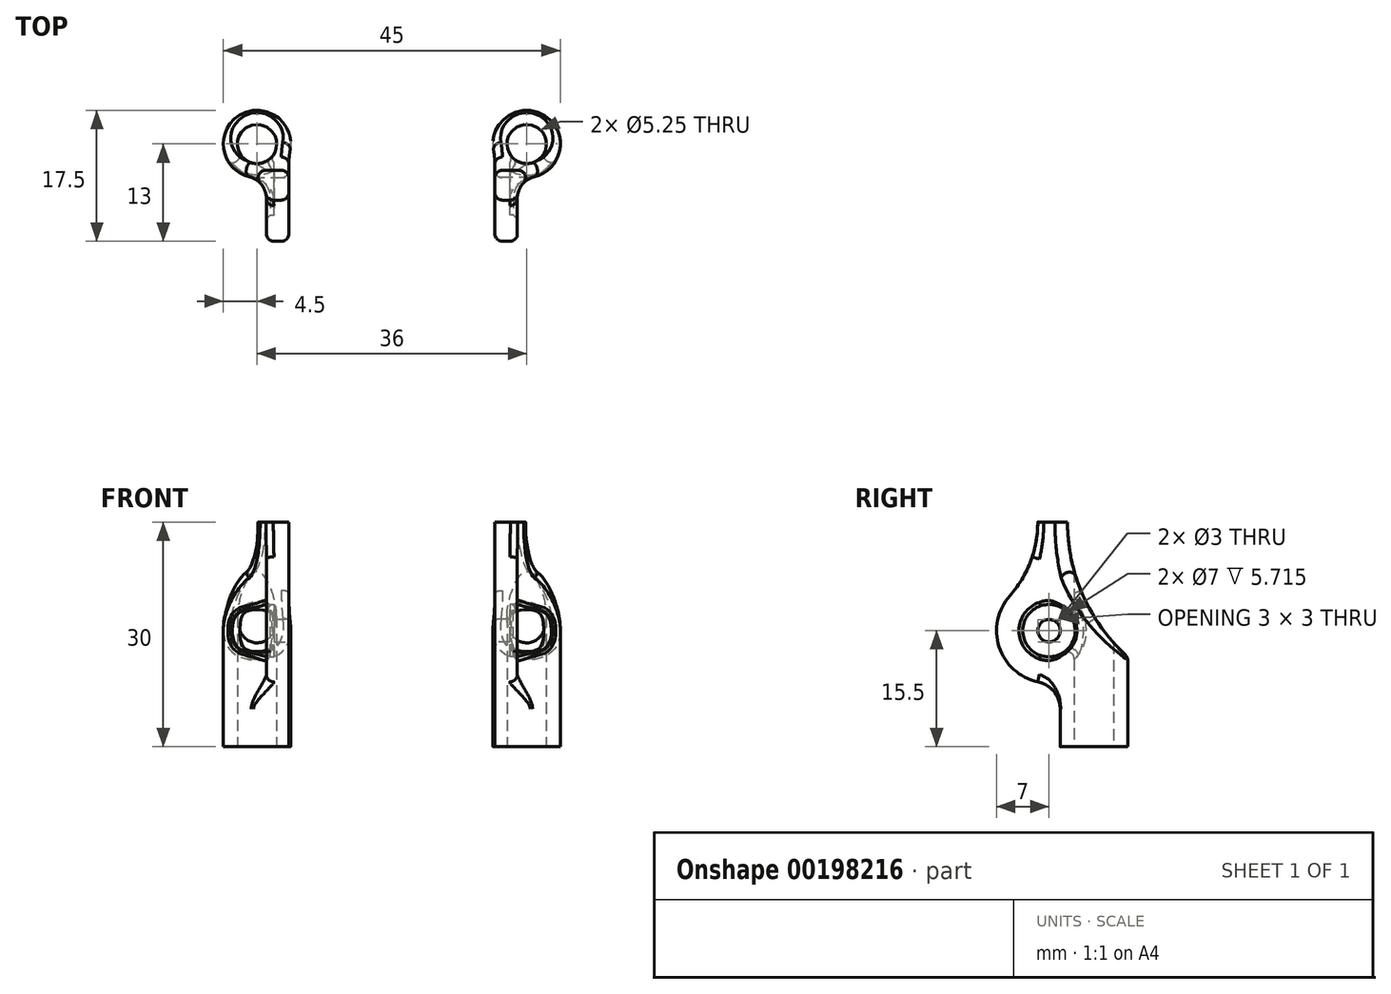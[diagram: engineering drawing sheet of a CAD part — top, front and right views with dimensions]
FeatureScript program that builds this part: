
annotation { "Feature Type Name" : "Feature", "Feature Type Description" : "" }
export const myFeature = defineFeature(function(context is Context, id is Id, definition is map)
    precondition{}
    {
        {
            var Q0;
            Q0=qCreatedBy(makeId("Top.planeOp"),FACE);
            var sketch = newSketch(context, id + "F0", { "sketchPlane" : qUnion([Q0])});
            skLineSegment(sketch, "E0", {"start": v(-13.75, 33.32) * mm, "end": v(-13.75, 22.5) * mm});
            skLineSegment(sketch, "E1", {"start": v(-13.75, 22.5) * mm, "end": v(-16.75, 22.5) * mm});
            skLineSegment(sketch, "E2", {"start": v(-16.75, 22.5) * mm, "end": v(-16.75, 28.7) * mm});
            skCircle(sketch, "E3", {"center": v(-18, 36) * mm, "radius": 2.62 * mm});
            skArc(sketch, "E4", {"start": v(-13.58, 35.17) * mm, "mid": v(-20.45, 39.78) * mm, "end": v(-19.05, 31.62) * mm});
            skPoint(sketch, "E5.visualSharp", {"position": v(-13.75, 34.52) * mm});
            skArc(sketch, "E5.filletArc", {"start": v(-13.58, 35.17) * mm, "mid": v(-13.7, 34.25) * mm, "end": v(-13.75, 33.32) * mm});
            skPoint(sketch, "E6.visualSharp", {"position": v(-16.75, 31.68) * mm});
            skArc(sketch, "E6.filletArc", {"start": v(-16.75, 28.7) * mm, "mid": v(-17.4, 30.56) * mm, "end": v(-19.05, 31.62) * mm});
            skSolve(sketch);
        }
        {
            var Q0;
            Q0=qSketchRegion(id+"F0",true);
            extrude(context, id + "F1", {"entities" : qUnion([Q0]), "depth" : 25 * mm});
        }
        {
            var Q0;
            Q0=makeQuery(id+"F1.opExtrude","SWEPT_FACE",FACE,{"disambiguationData":[OSD([sQuery(id+"F0.wireOp",EDGE,"E0")])]});
            var sketch = newSketch(context, id + "F2", { "sketchPlane" : qUnion([Q0])});
            skCircle(sketch, "E7", {"center": v(30, 10.5) * mm, "radius": 1.5 * mm});
            skArc(sketch, "E8", {"start": v(32.5, 26) * mm, "mid": v(34.36, 15.6) * mm, "end": v(40.5, 7) * mm});
            skLineSegment(sketch, "E9", {"start": v(32.5, 26) * mm, "end": v(40.5, 26) * mm});
            skLineSegment(sketch, "E10", {"start": v(40.5, 26) * mm, "end": v(40.5, 7) * mm});
            skLineSegment(sketch, "E11", {"start": v(28.5, 30) * mm, "end": v(28.5, 25) * mm});
            skArc(sketch, "E12", {"start": v(24.76, 15.14) * mm, "mid": v(27.53, 19.73) * mm, "end": v(28.5, 25) * mm});
            skArc(sketch, "E13", {"start": v(24.76, 15.14) * mm, "mid": v(23.35, 8.31) * mm, "end": v(28.54, 3.65) * mm});
            skLineSegment(sketch, "E14", {"start": v(28.5, 30) * mm, "end": v(18.5, 30) * mm});
            skLineSegment(sketch, "E15", {"start": v(18.5, 30) * mm, "end": v(18.5, -2) * mm});
            skArc(sketch, "E16", {"start": v(31.5, 0) * mm, "mid": v(30.67, 2.35) * mm, "end": v(28.54, 3.65) * mm});
            skLineSegment(sketch, "E17", {"start": v(31.5, 0) * mm, "end": v(31.5, -2) * mm});
            skLineSegment(sketch, "E18", {"start": v(31.5, -2) * mm, "end": v(18.5, -2) * mm});
            skSolve(sketch);
        }
        {
            var Q0;
            Q0=qSketchRegion(id+"F2",true);
            extrude(context, id + "F3", {"entities" : qUnion([Q0]), "operationType" : NewBodyOperationType.REMOVE, "oppositeDirection" : true, "depth" : 25 * mm, "hasSecondDirection" : true, "secondDirectionOppositeDirection" : false, "secondDirectionDepth" : 25 * mm});
        }
        {
            var Q0;
            Q0=makeQuery(id+"F1.opExtrude","SWEPT_FACE",FACE,{"disambiguationData":[OSD([sQuery(id+"F0.wireOp",EDGE,"E2")])]});
            var sketch = newSketch(context, id + "F4", { "sketchPlane" : qUnion([Q0])});
            skCircle(sketch, "E19", {"center": v(-30, 10.5) * mm, "radius": 3.5 * mm});
            skSolve(sketch);
        }
        {
            var Q0;
            Q0=qSketchRegion(id+"F4",true);
            extrude(context, id + "F5", {"entities" : qUnion([Q0]), "operationType" : NewBodyOperationType.REMOVE, "depth" : 6 * mm, "hasSecondDirection" : true, "secondDirectionOppositeDirection" : true, "secondDirectionDepth" : 1 * mm});
        }
        {
            var Q0;
            Q0=makeQuery(id+"F5.boolean.opBoolean","INTERSECT",EDGE,{"derivedFrom":[makeQuery(id+"F1.opExtrude","SWEPT_FACE",FACE,{"disambiguationData":[OSD([sQuery(id+"F0.wireOp",EDGE,"E2")])]}),makeQuery(id+"F5.opExtrude","SWEPT_FACE",FACE,{"disambiguationData":[OSD([sQuery(id+"F4.wireOp",EDGE,"E19")])]})]});
            chamfer(context, id + "F6", {"entities" : qUnion([Q0]), "width" : 0.5 * mm, "tangentPropagation" : true});
        }
        {
            var Q0;
            Q0=makeQuery(id+"F3.boolean.opBoolean","INTERSECT",EDGE,{"derivedFrom":[makeQuery(id+"F1.opExtrude","SWEPT_FACE",FACE,{"disambiguationData":[OSD([sQuery(id+"F0.wireOp",EDGE,"E2")])]}),makeQuery(id+"F3.opExtrude","SWEPT_FACE",FACE,{"disambiguationData":[OSD([sQuery(id+"F2.wireOp",EDGE,"E12")])]})]});
            var Q1;
            Q1=makeQuery(id+"F3.boolean.opBoolean","INTERSECT",EDGE,{"derivedFrom":[makeQuery(id+"F1.opExtrude","SWEPT_FACE",FACE,{"disambiguationData":[OSD([sQuery(id+"F0.wireOp",EDGE,"E0")])]}),makeQuery(id+"F3.opExtrude","SWEPT_FACE",FACE,{"disambiguationData":[OSD([sQuery(id+"F2.wireOp",EDGE,"E12")])]})]});
            var Q2;
            Q2=makeQuery(id+"F3.boolean.opBoolean","INTERSECT",EDGE,{"derivedFrom":[makeQuery(id+"F1.opExtrude","SWEPT_FACE",FACE,{"disambiguationData":[OSD([sQuery(id+"F0.wireOp",EDGE,"E4")])]}),makeQuery(id+"F3.opExtrude","SWEPT_FACE",FACE,{"disambiguationData":[OSD([sQuery(id+"F2.wireOp",EDGE,"E8")])]})]});
            var Q3;
            Q3=makeQuery(id+"F5.boolean.opBoolean","INTERSECT",EDGE,{"derivedFrom":[makeQuery(id+"F1.opExtrude","SWEPT_FACE",FACE,{"disambiguationData":[OSD([sQuery(id+"F0.wireOp",EDGE,"E3")])]}),makeQuery(id+"F5.opExtrude","SWEPT_FACE",FACE,{"disambiguationData":[OSD([sQuery(id+"F4.wireOp",EDGE,"E19")])]})]});
            fillet(context, id + "F7", {"entities" : qUnion([Q0, Q1, Q2, Q3]), "radius" : 1 * mm, "tangentPropagation" : true, "allowEdgeOverflow" : false});
        }
        {
            var Q0;
            Q0=makeQuery(id+"F1.opExtrude","SWEPT_BODY",BODY,{"disambiguationData":[OSD([sQuery(id+"F0.wireOp",EDGE,"E0"),sQuery(id+"F0.wireOp",EDGE,"E1"),sQuery(id+"F0.wireOp",EDGE,"E2"),sQuery(id+"F0.wireOp",EDGE,"E3"),sQuery(id+"F0.wireOp",EDGE,"E4"),sQuery(id+"F0.wireOp",EDGE,"E5.filletArc"),sQuery(id+"F0.wireOp",EDGE,"E6.filletArc")])]});
            var Q1;
            Q1=qCreatedBy(makeId("Right.planeOp"),FACE);
            mirror(context, id + "F8", {"entities" : qUnion([Q0]), "mirrorPlane" : qUnion([Q1])});
        }
        {
            var Q0;
            Q0=makeQuery(id+"F1.opExtrude","CAP_FACE",FACE,{"disambiguationData":[OSD([sQuery(id+"F0.wireOp",EDGE,"E0"),sQuery(id+"F0.wireOp",EDGE,"E1"),sQuery(id+"F0.wireOp",EDGE,"E2"),sQuery(id+"F0.wireOp",EDGE,"E3"),sQuery(id+"F0.wireOp",EDGE,"E4"),sQuery(id+"F0.wireOp",EDGE,"E5.filletArc"),sQuery(id+"F0.wireOp",EDGE,"E6.filletArc")])],"isStart":true});
            var Q1;
            Q1=makeQuery(id+"F8.opPattern","COPY",FACE,{"derivedFrom":makeQuery(id+"F1.opExtrude","CAP_FACE",FACE,{"disambiguationData":[OSD([sQuery(id+"F0.wireOp",EDGE,"E0"),sQuery(id+"F0.wireOp",EDGE,"E1"),sQuery(id+"F0.wireOp",EDGE,"E2"),sQuery(id+"F0.wireOp",EDGE,"E3"),sQuery(id+"F0.wireOp",EDGE,"E4"),sQuery(id+"F0.wireOp",EDGE,"E5.filletArc"),sQuery(id+"F0.wireOp",EDGE,"E6.filletArc")])],"isStart":true}),"instanceName":"1"});
            extrude(context, id + "F9", {"entities" : qUnion([Q0, Q1]), "operationType" : NewBodyOperationType.ADD, "depth" : 5 * mm});
        }
    });
